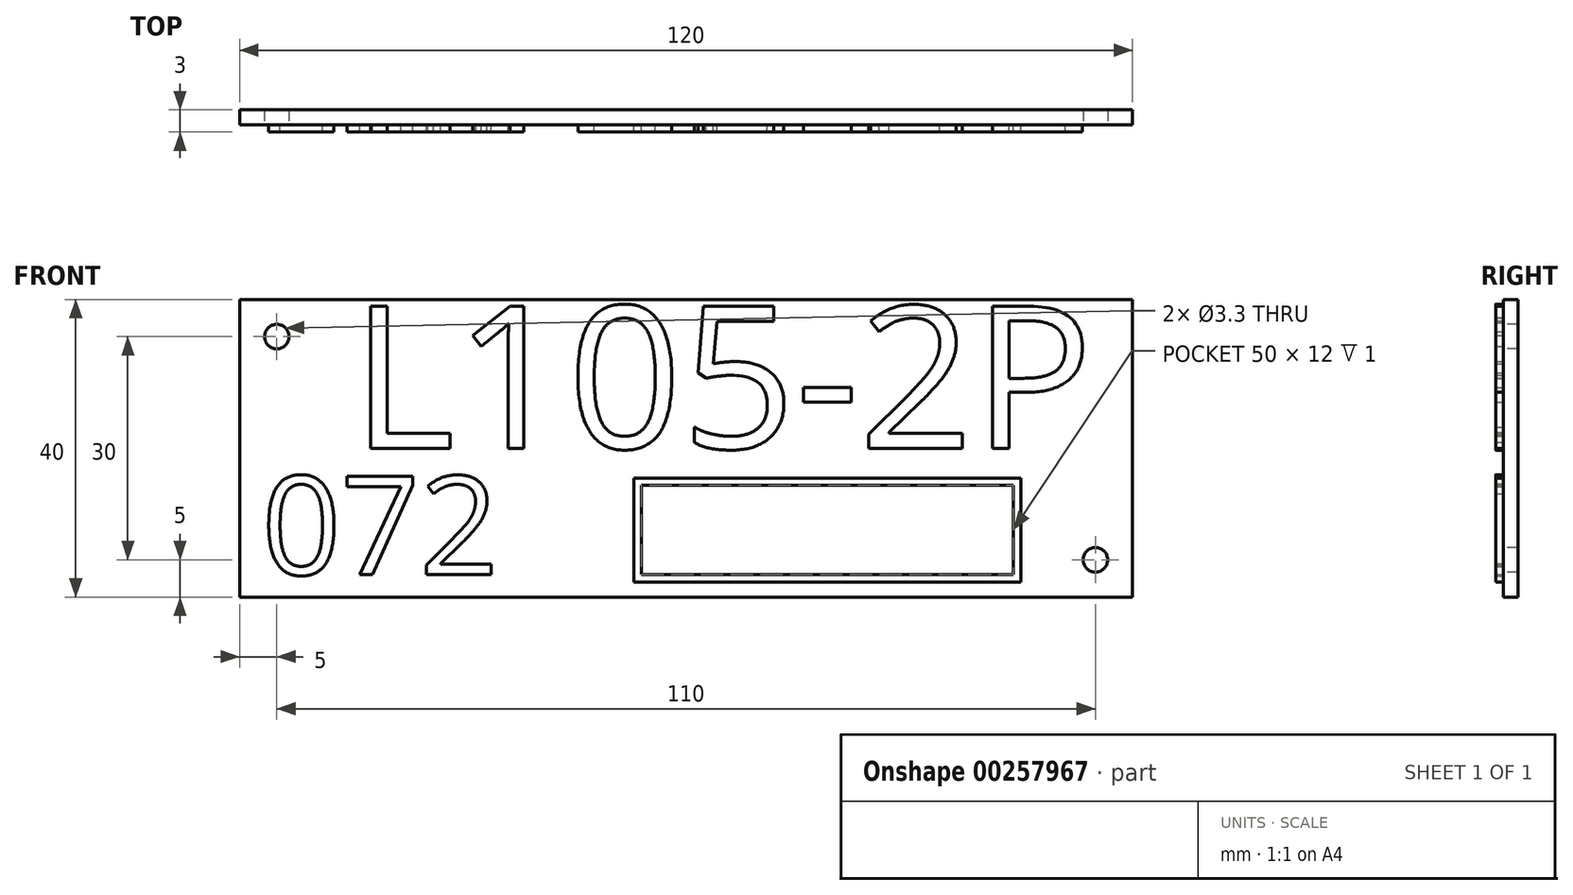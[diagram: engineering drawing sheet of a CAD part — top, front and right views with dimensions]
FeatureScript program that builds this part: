
annotation { "Feature Type Name" : "Feature", "Feature Type Description" : "" }
export const myFeature = defineFeature(function(context is Context, id is Id, definition is map)
    precondition{}
    {
        {
            var Q0;
            Q0=qCreatedBy(makeId("Front.planeOp"),FACE);
            var sketch = newSketch(context, id + "F0", { "sketchPlane" : qUnion([Q0])});
            skLineSegment(sketch, "E0.bottom", {"start": v(60, -20) * mm, "end": v(-60, -20) * mm});
            skLineSegment(sketch, "E0.top", {"start": v(60, 20) * mm, "end": v(-60, 20) * mm});
            skLineSegment(sketch, "E0.left", {"start": v(60, -20) * mm, "end": v(60, 20) * mm});
            skLineSegment(sketch, "E0.right", {"start": v(-60, -20) * mm, "end": v(-60, 20) * mm});
            skPoint(sketch, "E0.middle", {"position": v(0, 0) * mm});
            skSolve(sketch);
        }
        {
            var Q0;
            Q0=makeQuery(id+"F0.imprint","IMPRINT",FACE,{"disambiguationData":[TD([[makeQuery(id+"F0.imprint","IMPRINT",EDGE,{"derivedFrom":sQuery(id+"F0.wireOp",EDGE,"E0.bottom")}),-1.0]])]});
            extrude(context, id + "F1", {"entities" : qUnion([Q0]), "depth" : 2 * mm});
        }
        {
            var Q0;
            Q0=makeQuery(id+"F1.opExtrude","CAP_FACE",FACE,{"disambiguationData":[OSD([sQuery(id+"F0.wireOp",EDGE,"E0.bottom"),sQuery(id+"F0.wireOp",EDGE,"E0.top"),sQuery(id+"F0.wireOp",EDGE,"E0.left"),sQuery(id+"F0.wireOp",EDGE,"E0.right")])],"isStart":false});
            var sketch = newSketch(context, id + "F2", { "sketchPlane" : qUnion([Q0])});
            skPoint(sketch, "E1", {"position": v(-55, 15) * mm});
            skPoint(sketch, "E2", {"position": v(55, -15) * mm});
            skSolve(sketch);
        }
        {
            var Q0;
            Q0=sQuery(id+"F2.wireOp",VERTEX,"E1");
            var Q1;
            Q1=sQuery(id+"F2.wireOp",VERTEX,"E2");
            var Q2;
            Q2=makeQuery(id+"F1.opExtrude","SWEPT_BODY",BODY,{"disambiguationData":[OSD([sQuery(id+"F0.wireOp",EDGE,"E0.bottom"),sQuery(id+"F0.wireOp",EDGE,"E0.top"),sQuery(id+"F0.wireOp",EDGE,"E0.left"),sQuery(id+"F0.wireOp",EDGE,"E0.right")])]});
            hole(context, id + "F3", {"style" : HoleStyle.SIMPLE, "endStyle" : HoleEndStyle.THROUGH, "holeDiameter" : 3.3 * mm, "locations" : qUnion([Q0, Q1]), "scope" : qUnion([Q2]), "isTappedThrough" : true});
        }
        {
            var Q0;
            Q0=makeQuery(id+"F1.opExtrude","CAP_FACE",FACE,{"disambiguationData":[OSD([sQuery(id+"F0.wireOp",EDGE,"E0.bottom"),sQuery(id+"F0.wireOp",EDGE,"E0.top"),sQuery(id+"F0.wireOp",EDGE,"E0.left"),sQuery(id+"F0.wireOp",EDGE,"E0.right")])],"isStart":false});
            var sketch = newSketch(context, id + "F4", { "sketchPlane" : qUnion([Q0])});
            skText(sketch, "E3", { "text": "L105-2P", "fontName": "OpenSans-Regular.ttf"});
            const initialGuessF4  = {"E3": [-0.045, 0, 1, 0, 0.01923]};
            skSetInitialGuess(sketch, initialGuessF4);
            skSolve(sketch);
        }
        {
            var Q0;
            Q0=qSketchRegion(id+"F4",true);
            extrude(context, id + "F5", {"entities" : qUnion([Q0]), "operationType" : NewBodyOperationType.ADD, "depth" : 1 * mm});
        }
        {
            var Q0;
            {var subQ0=sQuery(id+"F0.wireOp",EDGE,"E0.top");var subQ1=sQuery(id+"F0.wireOp",EDGE,"E0.left");var subQ2=sQuery(id+"F0.wireOp",EDGE,"E0.right");var subQ3=sQuery(id+"F0.wireOp",EDGE,"E0.bottom");Q0=makeQuery(id+"F5.boolean.opBoolean","SPLIT",FACE,{"disambiguationData":[TD([makeQuery(id+"F1.opExtrude","SWEPT_FACE",FACE,{"disambiguationData":[OSD([subQ3])]})])],"derivedFrom":makeQuery(id+"F1.opExtrude","CAP_FACE",FACE,{"disambiguationData":[OSD([subQ3,subQ0,subQ1,subQ2])],"isStart":false})});}
            var sketch = newSketch(context, id + "F6", { "sketchPlane" : qUnion([Q0])});
            skText(sketch, "E4", { "text": "072", "fontName": "OpenSans-Regular.ttf"});
            const initialGuessF6  = {"E4": [-0.057, -0.017, 1, 0, 0.01335]};
            skSetInitialGuess(sketch, initialGuessF6);
            skSolve(sketch);
        }
        {
            var Q0;
            Q0=qSketchRegion(id+"F6",true);
            extrude(context, id + "F7", {"entities" : qUnion([Q0]), "operationType" : NewBodyOperationType.ADD, "depth" : 1 * mm});
        }
        {
            var Q0;
            {var subQ46=sQuery(id+"F0.wireOp",EDGE,"E0.top");var subQ48=sQuery(id+"F0.wireOp",EDGE,"E0.left");var subQ66=sQuery(id+"F0.wireOp",EDGE,"E0.right");var subQ76=sQuery(id+"F0.wireOp",EDGE,"E0.bottom");var subQ77=makeQuery(id+"F1.opExtrude","SWEPT_FACE",FACE,{"disambiguationData":[OSD([subQ76])]});Q0=makeQuery(id+"F7.boolean.opBoolean","SPLIT",FACE,{"disambiguationData":[TD([subQ77])],"derivedFrom":makeQuery(id+"F5.boolean.opBoolean","SPLIT",FACE,{"disambiguationData":[TD([subQ77])],"derivedFrom":makeQuery(id+"F1.opExtrude","CAP_FACE",FACE,{"disambiguationData":[OSD([subQ76,subQ46,subQ48,subQ66])],"isStart":false})})});}
            var sketch = newSketch(context, id + "F8", { "sketchPlane" : qUnion([Q0])});
            skLineSegment(sketch, "E5.bottom", {"start": v(45, -18) * mm, "end": v(-7, -18) * mm});
            skLineSegment(sketch, "E5.top", {"start": v(45, -4) * mm, "end": v(-7, -4) * mm});
            skLineSegment(sketch, "E5.left", {"start": v(45, -18) * mm, "end": v(45, -4) * mm});
            skLineSegment(sketch, "E5.right", {"start": v(-7, -18) * mm, "end": v(-7, -4) * mm});
            skPoint(sketch, "E5.middle", {"position": v(19, -11) * mm});
            skLineSegment(sketch, "E6.0", {"start": v(44, -5) * mm, "end": v(-6, -5) * mm});
            skLineSegment(sketch, "E6.1", {"start": v(44, -17) * mm, "end": v(44, -5) * mm});
            skLineSegment(sketch, "E6.2", {"start": v(44, -17) * mm, "end": v(-6, -17) * mm});
            skLineSegment(sketch, "E6.3", {"start": v(-6, -17) * mm, "end": v(-6, -5) * mm});
            skSolve(sketch);
        }
        {
            var Q0;
            Q0=makeQuery(id+"F8.imprint","IMPRINT",FACE,{"disambiguationData":[TD([[makeQuery(id+"F8.imprint","IMPRINT",EDGE,{"derivedFrom":sQuery(id+"F8.wireOp",EDGE,"E5.bottom")}),-1.0]])]});
            extrude(context, id + "F9", {"entities" : qUnion([Q0]), "operationType" : NewBodyOperationType.ADD, "depth" : 1 * mm});
        }
    });
